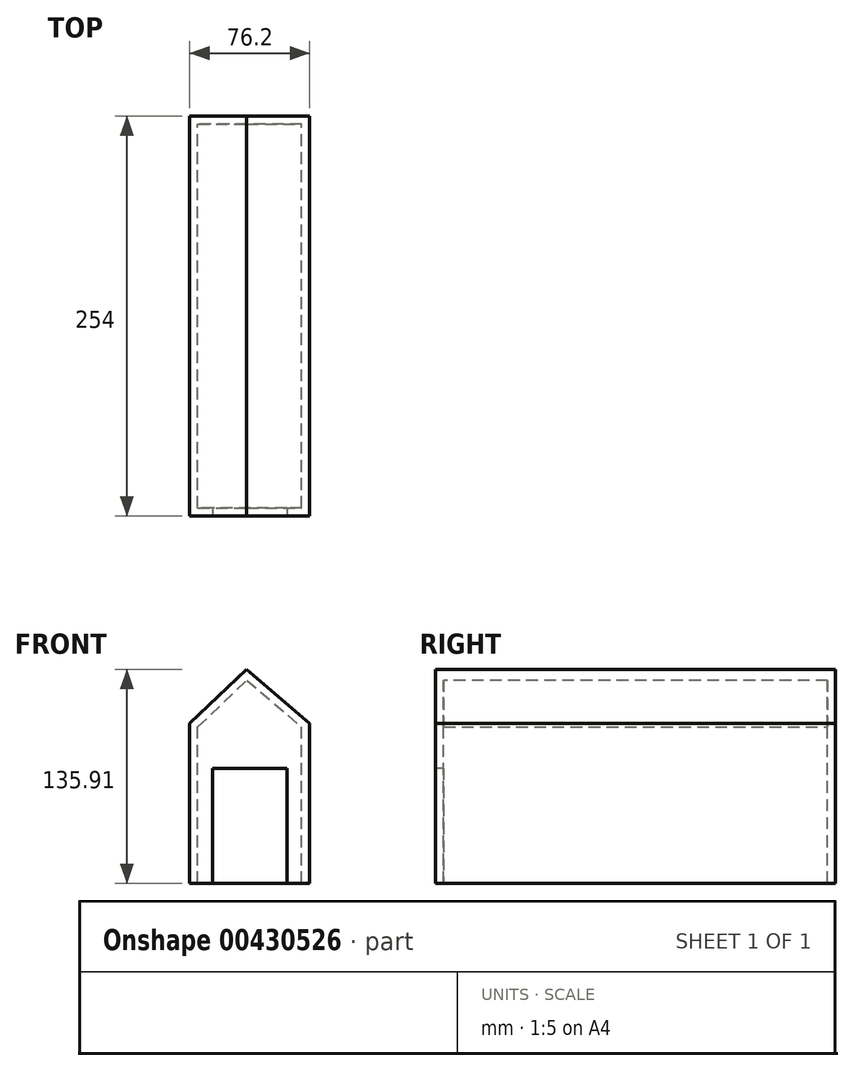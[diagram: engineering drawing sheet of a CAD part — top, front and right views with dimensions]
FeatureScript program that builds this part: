
annotation { "Feature Type Name" : "Feature", "Feature Type Description" : "" }
export const myFeature = defineFeature(function(context is Context, id is Id, definition is map)
    precondition{}
    {
        {
            var Q0;
            Q0=qCreatedBy(makeId("Front.planeOp"),FACE);
            var sketch = newSketch(context, id + "F0", { "sketchPlane" : qUnion([Q0])});
            skLineSegment(sketch, "E0.bottom", {"start": v(0, 0) * mm, "end": v(-76.2, 0) * mm});
            skLineSegment(sketch, "E0.top", {"start": v(0, 101.6) * mm, "end": v(-76.2, 101.6) * mm});
            skLineSegment(sketch, "E0.left", {"start": v(0, 0) * mm, "end": v(0, 101.6) * mm});
            skLineSegment(sketch, "E0.right", {"start": v(-76.2, 0) * mm, "end": v(-76.2, 101.6) * mm});
            skSolve(sketch);
        }
        {
            var Q0;
            Q0 = qSketchRegion(id + "F0", true);
            extrude(context, id + "F1", {"entities" : qUnion([Q0]), "depth" : 254 * mm});
        }
        {
            var Q0;
            Q0=makeQuery(id+"F1.opExtrude","CAP_FACE",FACE,{"disambiguationData":[OSD([sQuery(id+"F0.wireOp",EDGE,"E0.bottom"),sQuery(id+"F0.wireOp",EDGE,"E0.top"),sQuery(id+"F0.wireOp",EDGE,"E0.left"),sQuery(id+"F0.wireOp",EDGE,"E0.right")])],"isStart":false});
            var sketch = newSketch(context, id + "F2", { "sketchPlane" : qUnion([Q0])});
            skLineSegment(sketch, "E1", {"start": v(-76.2, 101.6) * mm, "end": v(-40.09, 135.9) * mm});
            skLineSegment(sketch, "E2", {"start": v(-40.09, 135.9) * mm, "end": v(0, 101.6) * mm});
            skLineSegment(sketch, "E3", {"start": v(-76.2, 101.6) * mm, "end": v(0, 101.6) * mm});
            skSolve(sketch);
        }
        {
            var Q0;
            Q0 = qSketchRegion(id + "F2", true);
            extrude(context, id + "F3", {"entities" : qUnion([Q0]), "operationType" : NewBodyOperationType.ADD, "oppositeDirection" : true, "depth" : 254 * mm});
        }
        {
            var Q0;
            Q0=makeQuery(id+"F1.opExtrude","SWEPT_FACE",FACE,{"disambiguationData":[OSD([sQuery(id+"F0.wireOp",EDGE,"E0.bottom")])]});
            shell(context, id + "F4", {"entities" : qUnion([Q0]), "thickness" : 5.08 * mm});
        }
        {
            var Q0;
            Q0=makeQuery(id+"F2.imprint","IMPRINT",FACE,{"disambiguationData":[TD([[makeQuery(id+"F2.imprint","IMPRINT",EDGE,{"derivedFrom":sQuery(id+"F2.wireOp",EDGE,"E3")}),1.0]])]});
            var sketch = newSketch(context, id + "F5", { "sketchPlane" : qUnion([Q0])});
            skLineSegment(sketch, "E4.bottom", {"start": v(-61.66, 0) * mm, "end": v(-14.54, 0) * mm});
            skLineSegment(sketch, "E4.top", {"start": v(-61.66, 73.16) * mm, "end": v(-14.54, 73.16) * mm});
            skLineSegment(sketch, "E4.left", {"start": v(-61.66, 0) * mm, "end": v(-61.66, 73.16) * mm});
            skLineSegment(sketch, "E4.right", {"start": v(-14.54, 0) * mm, "end": v(-14.54, 73.16) * mm});
            skSolve(sketch);
        }
        {
            var Q0;
            Q0 = qSketchRegion(id + "F5", true);
            extrude(context, id + "F6", {"entities" : qUnion([Q0]), "operationType" : NewBodyOperationType.REMOVE, "endBound" : BoundingType.UP_TO_NEXT, "oppositeDirection" : true, "depth" : 25.4 * mm});
        }
    });
